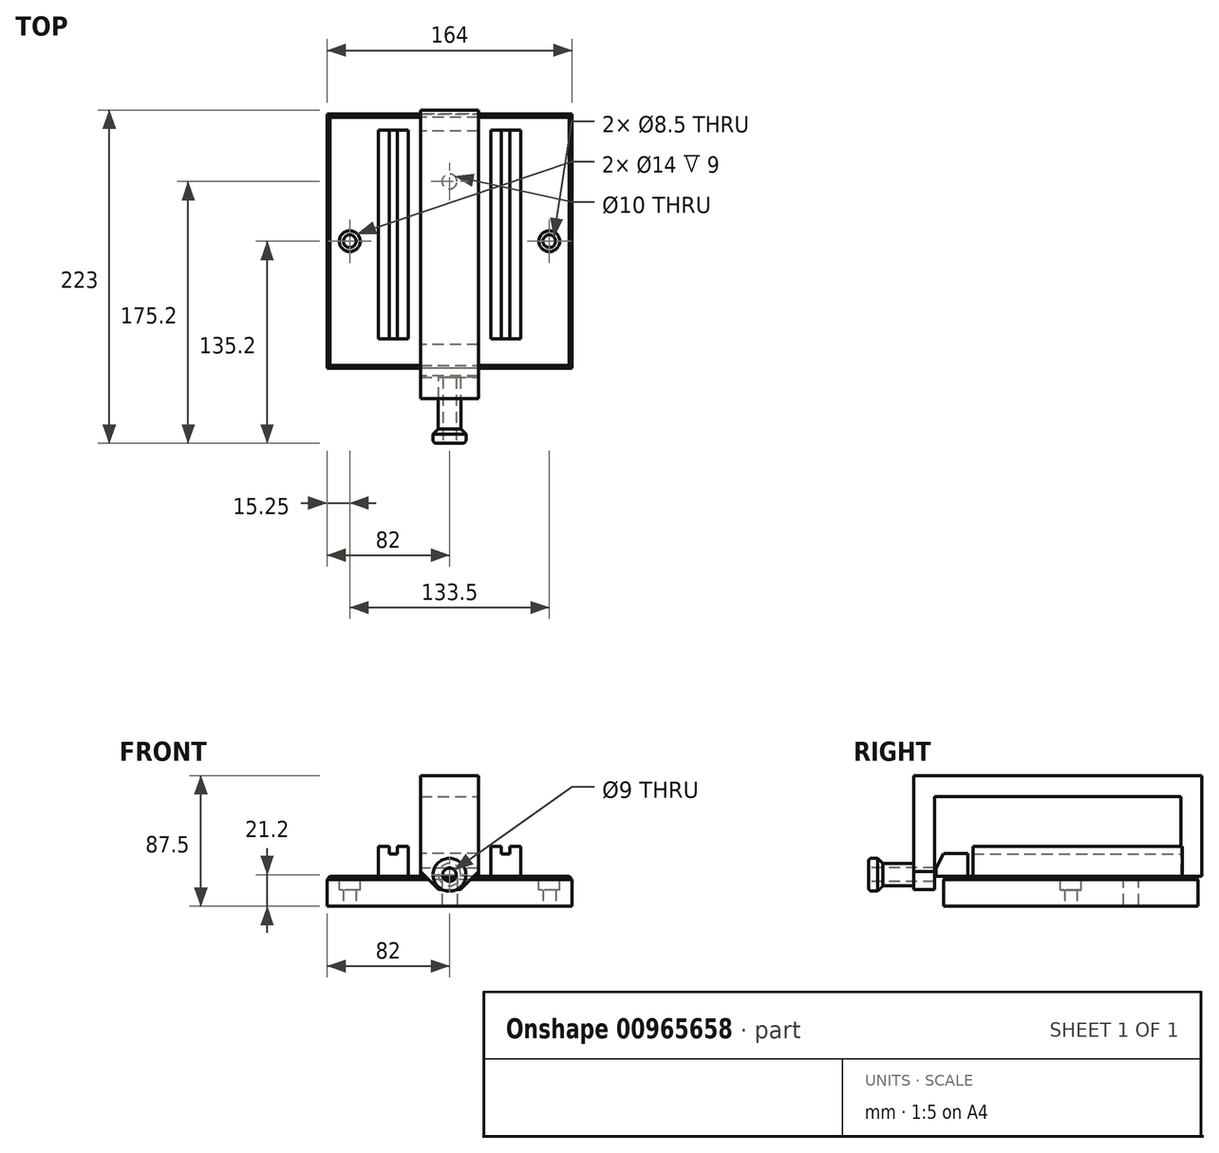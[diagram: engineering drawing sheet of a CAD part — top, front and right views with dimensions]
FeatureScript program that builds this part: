
annotation { "Feature Type Name" : "Feature", "Feature Type Description" : "" }
export const myFeature = defineFeature(function(context is Context, id is Id, definition is map)
    precondition{}
    {
        {
            var Q0;
            Q0=qCreatedBy(makeId("Top.planeOp"),FACE);
            var sketch = newSketch(context, id + "F0", { "sketchPlane" : qUnion([Q0])});
            skLineSegment(sketch, "E0.bottom", {"start": v(82, -85) * mm, "end": v(-82, -85) * mm});
            skLineSegment(sketch, "E0.top", {"start": v(82, 85) * mm, "end": v(-82, 85) * mm});
            skLineSegment(sketch, "E0.left", {"start": v(82, -85) * mm, "end": v(82, 85) * mm});
            skLineSegment(sketch, "E0.right", {"start": v(-82, -85) * mm, "end": v(-82, 85) * mm});
            skPoint(sketch, "E0.middle", {"position": v(0, 0) * mm});
            skCircle(sketch, "E1", {"center": v(-66.75, 0) * mm, "radius": 4.25 * mm});
            skPoint(sketch, "E1.centerSnap0", {"position": v(-82, 0) * mm});
            skCircle(sketch, "E2", {"center": v(66.75, 0) * mm, "radius": 4.25 * mm});
            skCircle(sketch, "E3", {"center": v(0, 40) * mm, "radius": 5 * mm});
            skSolve(sketch);
        }
        {
            var Q0;
            Q0=makeQuery(id+"F0.imprint","IMPRINT",FACE,{"disambiguationData":[TD([[makeQuery(id+"F0.imprint","IMPRINT",EDGE,{"derivedFrom":sQuery(id+"F0.wireOp",EDGE,"E0.bottom")}),-1.0]])]});
            extrude(context, id + "F1", {"entities" : qUnion([Q0]), "depth" : 20 * mm, "offsetDistance" : 25 * mm});
        }
        {
            var Q0;
            Q0=makeQuery(id+"F1.opExtrude","CAP_FACE",FACE,{"disambiguationData":[OSD([sQuery(id+"F0.wireOp",EDGE,"E0.bottom"),sQuery(id+"F0.wireOp",EDGE,"E0.top"),sQuery(id+"F0.wireOp",EDGE,"E0.left"),sQuery(id+"F0.wireOp",EDGE,"E0.right"),sQuery(id+"F0.wireOp",EDGE,"E1"),sQuery(id+"F0.wireOp",EDGE,"E2"),sQuery(id+"F0.wireOp",EDGE,"E3")])],"isStart":false});
            var sketch = newSketch(context, id + "F2", { "sketchPlane" : qUnion([Q0])});
            skCircle(sketch, "E4", {"center": v(-66.75, 0) * mm, "radius": 7 * mm});
            skCircle(sketch, "E5", {"center": v(66.75, 0) * mm, "radius": 7 * mm});
            skSolve(sketch);
        }
        {
            var Q0;
            Q0=makeQuery(id+"F1.opExtrude","CAP_EDGE",EDGE,{"disambiguationData":[OSD([sQuery(id+"F0.wireOp",EDGE,"E0.left")])],"isStart":false});
            var Q1;
            Q1=makeQuery(id+"F1.opExtrude","CAP_EDGE",EDGE,{"disambiguationData":[OSD([sQuery(id+"F0.wireOp",EDGE,"E0.bottom")])],"isStart":false});
            var Q2;
            Q2=makeQuery(id+"F1.opExtrude","CAP_EDGE",EDGE,{"disambiguationData":[OSD([sQuery(id+"F0.wireOp",EDGE,"E0.top")])],"isStart":false});
            var Q3;
            Q3=makeQuery(id+"F1.opExtrude","CAP_EDGE",EDGE,{"disambiguationData":[OSD([sQuery(id+"F0.wireOp",EDGE,"E0.right")])],"isStart":false});
            chamfer(context, id + "F3", {"entities" : qUnion([Q0, Q1, Q2, Q3]), "width" : 2 * mm, "tangentPropagation" : true});
        }
        {
            var Q0;
            Q0=makeQuery(id+"F0.imprint","IMPRINT",FACE,{"disambiguationData":[TD([[makeQuery(id+"F0.imprint","IMPRINT",EDGE,{"derivedFrom":sQuery(id+"F0.wireOp",EDGE,"E3")}),1.0]])]});
            extrude(context, id + "F4", {"entities" : qUnion([Q0]), "operationType" : NewBodyOperationType.REMOVE, "depth" : 20 * mm, "offsetDistance" : 25 * mm});
        }
        {
            var Q0;
            Q0=makeQuery(id+"F2.imprint","IMPRINT",FACE,{"disambiguationData":[TD([[makeQuery(id+"F2.imprint","IMPRINT",EDGE,{"derivedFrom":sQuery(id+"F2.wireOp",EDGE,"E4")}),1.0]])]});
            var Q1;
            Q1=makeQuery(id+"F2.imprint","IMPRINT",FACE,{"disambiguationData":[TD([[makeQuery(id+"F2.imprint","IMPRINT",EDGE,{"derivedFrom":sQuery(id+"F2.wireOp",EDGE,"E5")}),1.0]])]});
            var Q2;
            Q2=sQuery(id+"F2.wireOp",EDGE,"E4");
            var Q3;
            Q3=sQuery(id+"F2.wireOp",EDGE,"E5");
            extrude(context, id + "F5", {"entities" : qUnion([Q0, Q1]), "operationType" : NewBodyOperationType.REMOVE, "surfaceEntities" : qUnion([Q2, Q3]), "oppositeDirection" : true, "depth" : 9 * mm, "offsetDistance" : 25 * mm});
        }
        {
            var Q0;
            Q0=makeQuery(id+"F2.imprint","IMPRINT",FACE,{"disambiguationData":[TD([[makeQuery(id+"F2.imprint","IMPRINT",EDGE,{"derivedFrom":sQuery(id+"F2.wireOp",EDGE,"E4")}),-1.0]])]});
            var sketch = newSketch(context, id + "F6", { "sketchPlane" : qUnion([Q0])});
            skLineSegment(sketch, "E6.bottom", {"start": v(-47.5, 74.5) * mm, "end": v(-27.5, 74.5) * mm});
            skLineSegment(sketch, "E6.top", {"start": v(-47.5, -65.5) * mm, "end": v(-27.5, -65.5) * mm});
            skLineSegment(sketch, "E6.left", {"start": v(-47.5, 74.5) * mm, "end": v(-47.5, -65.5) * mm});
            skLineSegment(sketch, "E6.right", {"start": v(-27.5, 74.5) * mm, "end": v(-27.5, -65.5) * mm});
            skLineSegment(sketch, "E7.MirrorCS", {"start": v(27.5, 74.5) * mm, "end": v(27.5, -65.5) * mm});
            skLineSegment(sketch, "E8.MirrorCS", {"start": v(47.5, 74.5) * mm, "end": v(27.5, 74.5) * mm});
            skLineSegment(sketch, "E9.MirrorCS", {"start": v(47.5, 74.5) * mm, "end": v(47.5, -65.5) * mm});
            skLineSegment(sketch, "E10.MirrorCS", {"start": v(47.5, -65.5) * mm, "end": v(27.5, -65.5) * mm});
            skSolve(sketch);
        }
        {
            var Q0;
            Q0=makeQuery(id+"F6.imprint","IMPRINT",FACE,{"disambiguationData":[TD([[makeQuery(id+"F6.imprint","IMPRINT",EDGE,{"derivedFrom":sQuery(id+"F6.wireOp",EDGE,"E6.bottom")}),-1.0]])]});
            var Q1;
            Q1=makeQuery(id+"F6.imprint","IMPRINT",FACE,{"disambiguationData":[TD([[makeQuery(id+"F6.imprint","IMPRINT",EDGE,{"derivedFrom":sQuery(id+"F6.wireOp",EDGE,"E7.MirrorCS")}),1.0]])]});
            extrude(context, id + "F7", {"entities" : qUnion([Q0, Q1]), "operationType" : NewBodyOperationType.ADD, "depth" : 20 * mm, "offsetDistance" : 25 * mm});
        }
        {
            var Q0;
            Q0=makeQuery(id+"F7.opExtrude","CAP_FACE",FACE,{"disambiguationData":[OSD([sQuery(id+"F6.wireOp",EDGE,"E6.bottom"),sQuery(id+"F6.wireOp",EDGE,"E6.top"),sQuery(id+"F6.wireOp",EDGE,"E6.left"),sQuery(id+"F6.wireOp",EDGE,"E6.right")])],"isStart":false});
            var sketch = newSketch(context, id + "F8", { "sketchPlane" : qUnion([Q0])});
            skLineSegment(sketch, "E11.bottom", {"start": v(-34.75, -65.5) * mm, "end": v(-40.25, -65.5) * mm});
            skLineSegment(sketch, "E11.top", {"start": v(-34.75, 74.5) * mm, "end": v(-40.25, 74.5) * mm});
            skLineSegment(sketch, "E11.left", {"start": v(-34.75, -65.5) * mm, "end": v(-34.75, 74.5) * mm});
            skLineSegment(sketch, "E11.right", {"start": v(-40.25, -65.5) * mm, "end": v(-40.25, 74.5) * mm});
            skPoint(sketch, "E11.middle", {"position": v(-37.5, 4.5) * mm});
            skPoint(sketch, "E11.middle.positionSnap0", {"position": v(-27.5, 4.5) * mm});
            skPoint(sketch, "E11.middle.positionSnap1", {"position": v(-37.5, 74.5) * mm});
            skPoint(sketch, "E11.centerSnap0", {"position": v(-27.5, 4.5) * mm});
            skPoint(sketch, "E11.centerSnap1", {"position": v(-37.5, 74.5) * mm});
            skLineSegment(sketch, "E12.MirrorCS", {"start": v(34.75, -65.5) * mm, "end": v(34.75, 74.5) * mm});
            skLineSegment(sketch, "E13.MirrorCS", {"start": v(40.25, -65.5) * mm, "end": v(40.25, 74.5) * mm});
            skLineSegment(sketch, "E14.MirrorCS", {"start": v(34.75, 74.5) * mm, "end": v(40.25, 74.5) * mm});
            skLineSegment(sketch, "E15.MirrorCS", {"start": v(34.75, -65.5) * mm, "end": v(40.25, -65.5) * mm});
            skSolve(sketch);
        }
        {
            var Q0;
            Q0=makeQuery(id+"F8.imprint","IMPRINT",FACE,{"disambiguationData":[TD([[makeQuery(id+"F8.imprint","IMPRINT",EDGE,{"derivedFrom":sQuery(id+"F8.wireOp",EDGE,"E11.bottom")}),1.0]])]});
            var Q1;
            Q1=makeQuery(id+"F8.imprint","IMPRINT",FACE,{"disambiguationData":[TD([[makeQuery(id+"F8.imprint","IMPRINT",EDGE,{"derivedFrom":sQuery(id+"F8.wireOp",EDGE,"E12.MirrorCS")}),-1.0]])]});
            extrude(context, id + "F9", {"entities" : qUnion([Q0, Q1]), "operationType" : NewBodyOperationType.REMOVE, "oppositeDirection" : true, "depth" : 5 * mm, "offsetDistance" : 25 * mm});
        }
        {
            var Q0;
            Q0=makeQuery(id+"F2.imprint","IMPRINT",FACE,{"disambiguationData":[TD([[makeQuery(id+"F2.imprint","IMPRINT",EDGE,{"derivedFrom":sQuery(id+"F2.wireOp",EDGE,"E4")}),-1.0]])]});
            var sketch = newSketch(context, id + "F10", { "sketchPlane" : qUnion([Q0])});
            skLineSegment(sketch, "E16.bottom", {"start": v(19.25, 73.8) * mm, "end": v(-19.25, 73.8) * mm});
            skLineSegment(sketch, "E16.top", {"start": v(19.25, 87.8) * mm, "end": v(-19.25, 87.8) * mm});
            skLineSegment(sketch, "E16.left", {"start": v(19.25, 73.8) * mm, "end": v(19.25, 87.8) * mm});
            skLineSegment(sketch, "E16.right", {"start": v(-19.25, 73.8) * mm, "end": v(-19.25, 87.8) * mm});
            skPoint(sketch, "E16.middle", {"position": v(0, 80.8) * mm});
            skSolve(sketch);
        }
        {
            var Q0;
            {var subQ0=sQuery(id+"F10.wireOp",EDGE,"E16.top");Q0=makeQuery(id+"F10.imprint","IMPRINT",FACE,{"disambiguationData":[TD([[makeQuery(id+"F10.imprint","IMPRINT",EDGE,{"derivedFrom":subQ0}),1.0]])]});}
            var Q1;
            {var subQ0=sQuery(id+"F10.wireOp",EDGE,"E16.bottom");Q1=makeQuery(id+"F10.imprint","IMPRINT",FACE,{"disambiguationData":[TD([[makeQuery(id+"F10.imprint","IMPRINT",EDGE,{"derivedFrom":subQ0}),-1.0]])]});}
            extrude(context, id + "F11", {"entities" : qUnion([Q0, Q1]), "operationType" : NewBodyOperationType.ADD, "depth" : 67.5 * mm, "offsetDistance" : 25 * mm});
        }
        {
            var Q0;
            Q0=makeQuery(id+"F11.opExtrude","SWEPT_FACE",FACE,{"disambiguationData":[OSD([sQuery(id+"F10.wireOp",EDGE,"E16.bottom")])]});
            var sketch = newSketch(context, id + "F12", { "sketchPlane" : qUnion([Q0])});
            skLineSegment(sketch, "E17.bottom", {"start": v(-19.25, 87.5) * mm, "end": v(19.25, 87.5) * mm});
            skLineSegment(sketch, "E17.top", {"start": v(-19.25, 73.5) * mm, "end": v(19.25, 73.5) * mm});
            skLineSegment(sketch, "E17.left", {"start": v(-19.25, 87.5) * mm, "end": v(-19.25, 73.5) * mm});
            skLineSegment(sketch, "E17.right", {"start": v(19.25, 87.5) * mm, "end": v(19.25, 73.5) * mm});
            skSolve(sketch);
        }
        {
            var Q0;
            Q0=makeQuery(id+"F12.imprint","IMPRINT",FACE,{"disambiguationData":[TD([[makeQuery(id+"F12.imprint","IMPRINT",EDGE,{"derivedFrom":sQuery(id+"F12.wireOp",EDGE,"E17.bottom")}),1.0]])]});
            extrude(context, id + "F13", {"entities" : qUnion([Q0]), "operationType" : NewBodyOperationType.ADD, "depth" : 179 * mm, "offsetDistance" : 25 * mm});
        }
        {
            var Q0;
            Q0=makeQuery(id+"F13.opExtrude","SWEPT_FACE",FACE,{"disambiguationData":[OSD([sQuery(id+"F12.wireOp",EDGE,"E17.top")])]});
            var sketch = newSketch(context, id + "F14", { "sketchPlane" : qUnion([Q0])});
            skLineSegment(sketch, "E18.bottom", {"start": v(-19.25, 105.2) * mm, "end": v(19.25, 105.2) * mm});
            skLineSegment(sketch, "E18.top", {"start": v(-19.25, 91.2) * mm, "end": v(19.25, 91.2) * mm});
            skLineSegment(sketch, "E18.left", {"start": v(-19.25, 105.2) * mm, "end": v(-19.25, 91.2) * mm});
            skLineSegment(sketch, "E18.right", {"start": v(19.25, 105.2) * mm, "end": v(19.25, 91.2) * mm});
            skSolve(sketch);
        }
        {
            var Q0;
            Q0 = qSketchRegion(id + "F14", true);
            var Q1;
            Q1=makeQuery(id+"F14.imprint","IMPRINT",FACE,{"disambiguationData":[TD([[makeQuery(id+"F14.imprint","IMPRINT",EDGE,{"derivedFrom":sQuery(id+"F14.wireOp",EDGE,"E18.bottom")}),-1.0]])]});
            extrude(context, id + "F15", {"entities" : qUnion([Q0, Q1]), "operationType" : NewBodyOperationType.ADD, "depth" : 62.2 * mm, "offsetDistance" : 25 * mm});
        }
        {
            var Q0;
            Q0=makeQuery(id+"F15.opExtrude","CAP_EDGE",EDGE,{"disambiguationData":[OSD([sQuery(id+"F14.wireOp",EDGE,"E18.left")])],"isStart":false});
            var Q1;
            Q1=makeQuery(id+"F15.opExtrude","CAP_EDGE",EDGE,{"disambiguationData":[OSD([sQuery(id+"F14.wireOp",EDGE,"E18.right")])],"isStart":false});
            chamfer(context, id + "F16", {"entities" : qUnion([Q0, Q1]), "width" : 12 * mm, "tangentPropagation" : true});
        }
        {
            var Q0;
            Q0=makeQuery(id+"F15.boolean.opBoolean","MERGE",FACE,{"derivedFrom":[makeQuery(id+"F13.opExtrude","CAP_FACE",FACE,{"disambiguationData":[OSD([sQuery(id+"F12.wireOp",EDGE,"E17.bottom"),sQuery(id+"F12.wireOp",EDGE,"E17.top"),sQuery(id+"F12.wireOp",EDGE,"E17.left"),sQuery(id+"F12.wireOp",EDGE,"E17.right")])],"isStart":false}),makeQuery(id+"F15.opExtrude","SWEPT_FACE",FACE,{"disambiguationData":[OSD([sQuery(id+"F14.wireOp",EDGE,"E18.bottom")])]})]});
            var sketch = newSketch(context, id + "F17", { "sketchPlane" : qUnion([Q0])});
            skCircle(sketch, "E19", {"center": v(0, 21.2) * mm, "radius": 4.5 * mm});
            skPoint(sketch, "E19.centerSnap0", {"position": v(0, 11.3) * mm});
            skSolve(sketch);
        }
        {
            var Q0;
            Q0=makeQuery(id+"F17.imprint","IMPRINT",FACE,{"disambiguationData":[TD([[makeQuery(id+"F17.imprint","IMPRINT",EDGE,{"derivedFrom":sQuery(id+"F17.wireOp",EDGE,"E19")}),1.0]])]});
            extrude(context, id + "F18", {"entities" : qUnion([Q0]), "operationType" : NewBodyOperationType.REMOVE, "oppositeDirection" : true, "depth" : 14 * mm, "offsetDistance" : 25 * mm});
        }
        {
            var Q0;
            Q0=makeQuery(id+"F15.boolean.opBoolean","MERGE",FACE,{"derivedFrom":[makeQuery(id+"F13.opExtrude","CAP_FACE",FACE,{"disambiguationData":[OSD([sQuery(id+"F12.wireOp",EDGE,"E17.bottom"),sQuery(id+"F12.wireOp",EDGE,"E17.top"),sQuery(id+"F12.wireOp",EDGE,"E17.left"),sQuery(id+"F12.wireOp",EDGE,"E17.right")])],"isStart":false}),makeQuery(id+"F15.opExtrude","SWEPT_FACE",FACE,{"disambiguationData":[OSD([sQuery(id+"F14.wireOp",EDGE,"E18.bottom")])]})]});
            var sketch = newSketch(context, id + "F19", { "sketchPlane" : qUnion([Q0])});
            skCircle(sketch, "E20", {"center": v(0, 21.2) * mm, "radius": 7.5 * mm});
            skSolve(sketch);
        }
        {
            var Q0;
            Q0=makeQuery(id+"F19.imprint","IMPRINT",FACE,{"disambiguationData":[TD([[makeQuery(id+"F19.imprint","IMPRINT",EDGE,{"derivedFrom":sQuery(id+"F19.wireOp",EDGE,"E20")}),1.0]])]});
            var Q1;
            Q1=makeQuery(id+"F19.imprint","IMPRINT",FACE,{"disambiguationData":[TD([[makeQuery(id+"F19.imprint","IMPRINT",EDGE,{"derivedFrom":makeQuery(id+"F18.boolean.opBoolean","COPY",EDGE,{"derivedFrom":makeQuery(id+"F18.opExtrude","CAP_EDGE",EDGE,{"disambiguationData":[OSD([sQuery(id+"F17.wireOp",EDGE,"E19")])],"isStart":true})})}),1.0]])]});
            extrude(context, id + "F20", {"entities" : qUnion([Q0, Q1]), "operationType" : NewBodyOperationType.ADD, "depth" : 19 * mm, "offsetDistance" : 25 * mm});
        }
        {
            var Q0;
            Q0=makeQuery(id+"F20.opExtrude","CAP_FACE",FACE,{"disambiguationData":[OSD([sQuery(id+"F19.wireOp",EDGE,"E20")])],"isStart":false});
            var sketch = newSketch(context, id + "F21", { "sketchPlane" : qUnion([Q0])});
            skCircle(sketch, "E21", {"center": v(0, 21.2) * mm, "radius": 11 * mm});
            skSolve(sketch);
        }
        {
            var Q0;
            Q0=makeQuery(id+"F21.imprint","IMPRINT",FACE,{"disambiguationData":[TD([[makeQuery(id+"F21.imprint","IMPRINT",EDGE,{"derivedFrom":sQuery(id+"F21.wireOp",EDGE,"E21")}),1.0]])]});
            var Q1;
            Q1=makeQuery(id+"F21.imprint","IMPRINT",FACE,{"disambiguationData":[TD([[makeQuery(id+"F21.imprint","IMPRINT",EDGE,{"derivedFrom":makeQuery(id+"F20.opExtrude","CAP_EDGE",EDGE,{"disambiguationData":[OSD([sQuery(id+"F19.wireOp",EDGE,"E20")])],"isStart":false})}),1.0]])]});
            extrude(context, id + "F22", {"entities" : qUnion([Q0, Q1]), "operationType" : NewBodyOperationType.ADD, "depth" : 11 * mm, "offsetDistance" : 25 * mm});
        }
        {
            var Q0;
            Q0=makeQuery(id+"F22.opExtrude","CAP_EDGE",EDGE,{"disambiguationData":[OSD([sQuery(id+"F21.wireOp",EDGE,"E21")])],"isStart":true});
            chamfer(context, id + "F23", {"entities" : qUnion([Q0]), "width" : 5 * mm, "tangentPropagation" : true});
        }
        {
            var Q0;
            Q0=makeQuery(id+"F22.opExtrude","CAP_EDGE",EDGE,{"disambiguationData":[OSD([sQuery(id+"F21.wireOp",EDGE,"E21")])],"isStart":false});
            fillet(context, id + "F24", {"entities" : qUnion([Q0]), "radius" : 2 * mm, "tangentPropagation" : true, "allowEdgeOverflow" : false});
        }
        {
            var Q0;
            Q0=makeQuery(id+"F2.imprint","IMPRINT",FACE,{"disambiguationData":[TD([[makeQuery(id+"F2.imprint","IMPRINT",EDGE,{"derivedFrom":sQuery(id+"F2.wireOp",EDGE,"E4")}),-1.0]])]});
            var sketch = newSketch(context, id + "F25", { "sketchPlane" : qUnion([Q0])});
            skLineSegment(sketch, "E22.bottom", {"start": v(19.25, -90) * mm, "end": v(-19.25, -90) * mm});
            skLineSegment(sketch, "E22.top", {"start": v(19.25, -69) * mm, "end": v(-19.25, -69) * mm});
            skLineSegment(sketch, "E22.left", {"start": v(19.25, -90) * mm, "end": v(19.25, -69) * mm});
            skLineSegment(sketch, "E22.right", {"start": v(-19.25, -90) * mm, "end": v(-19.25, -69) * mm});
            skPoint(sketch, "E22.middle", {"position": v(0, -79.5) * mm});
            skSolve(sketch);
        }
        {
            var Q0;
            {var subQ0=sQuery(id+"F25.wireOp",EDGE,"E22.top");Q0=makeQuery(id+"F25.imprint","IMPRINT",FACE,{"disambiguationData":[TD([[makeQuery(id+"F25.imprint","IMPRINT",EDGE,{"derivedFrom":subQ0}),1.0]])]});}
            var Q1;
            {var subQ0=sQuery(id+"F25.wireOp",EDGE,"E22.bottom");Q1=makeQuery(id+"F25.imprint","IMPRINT",FACE,{"disambiguationData":[TD([[makeQuery(id+"F25.imprint","IMPRINT",EDGE,{"derivedFrom":subQ0}),-1.0]])]});}
            extrude(context, id + "F26", {"entities" : qUnion([Q0, Q1]), "operationType" : NewBodyOperationType.ADD, "depth" : 15.5 * mm, "offsetDistance" : 25 * mm});
        }
        {
            var Q0;
            Q0=makeQuery(id+"F26.opExtrude","CAP_EDGE",EDGE,{"disambiguationData":[OSD([sQuery(id+"F25.wireOp",EDGE,"E22.bottom")])],"isStart":false});
            chamfer(context, id + "F27", {"entities" : qUnion([Q0]), "chamferType" : ChamferType.TWO_OFFSETS, "width1" : 10 * mm, "oppositeDirection" : false, "width2" : 5 * mm, "tangentPropagation" : true});
        }
    });
